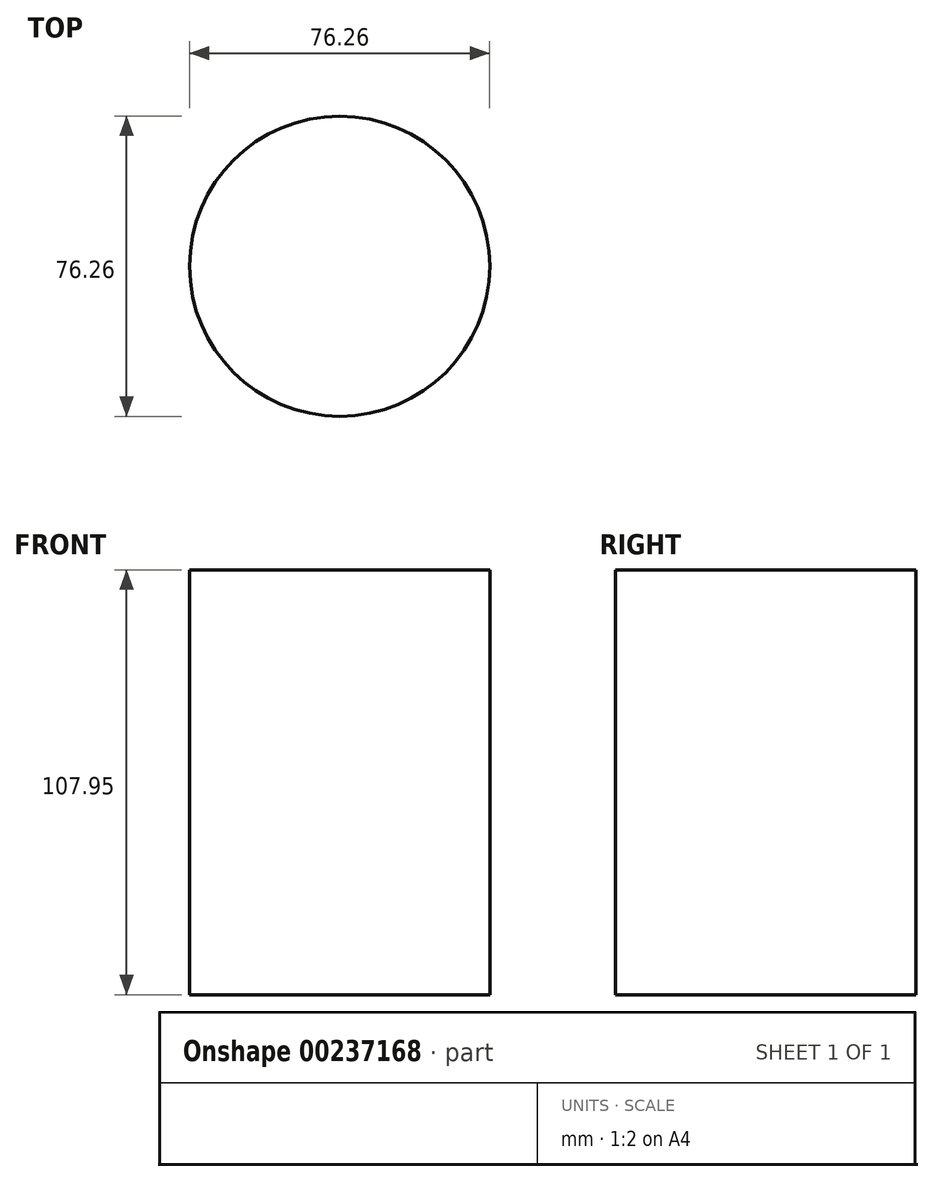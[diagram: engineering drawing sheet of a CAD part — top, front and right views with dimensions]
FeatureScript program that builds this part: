
annotation { "Feature Type Name" : "Feature", "Feature Type Description" : "" }
export const myFeature = defineFeature(function(context is Context, id is Id, definition is map)
    precondition{}
    {
        {
            var Q0;
            Q0=qCreatedBy(makeId("Top.planeOp"),FACE);
            var sketch = newSketch(context, id + "F0", { "sketchPlane" : qUnion([Q0])});
            skCircle(sketch, "E0", {"center": v(0, 0) * mm, "radius": 38.13 * mm});
            skSolve(sketch);
        }
        {
            var Q0;
            Q0=makeQuery(id+"F0.imprint","IMPRINT",FACE,{"disambiguationData":[TD([[makeQuery(id+"F0.imprint","IMPRINT",EDGE,{"derivedFrom":sQuery(id+"F0.wireOp",EDGE,"E0")}),1.0]])]});
            extrude(context, id + "F1", {"entities" : qUnion([Q0]), "depth" : 107.95 * mm});
        }
    });
